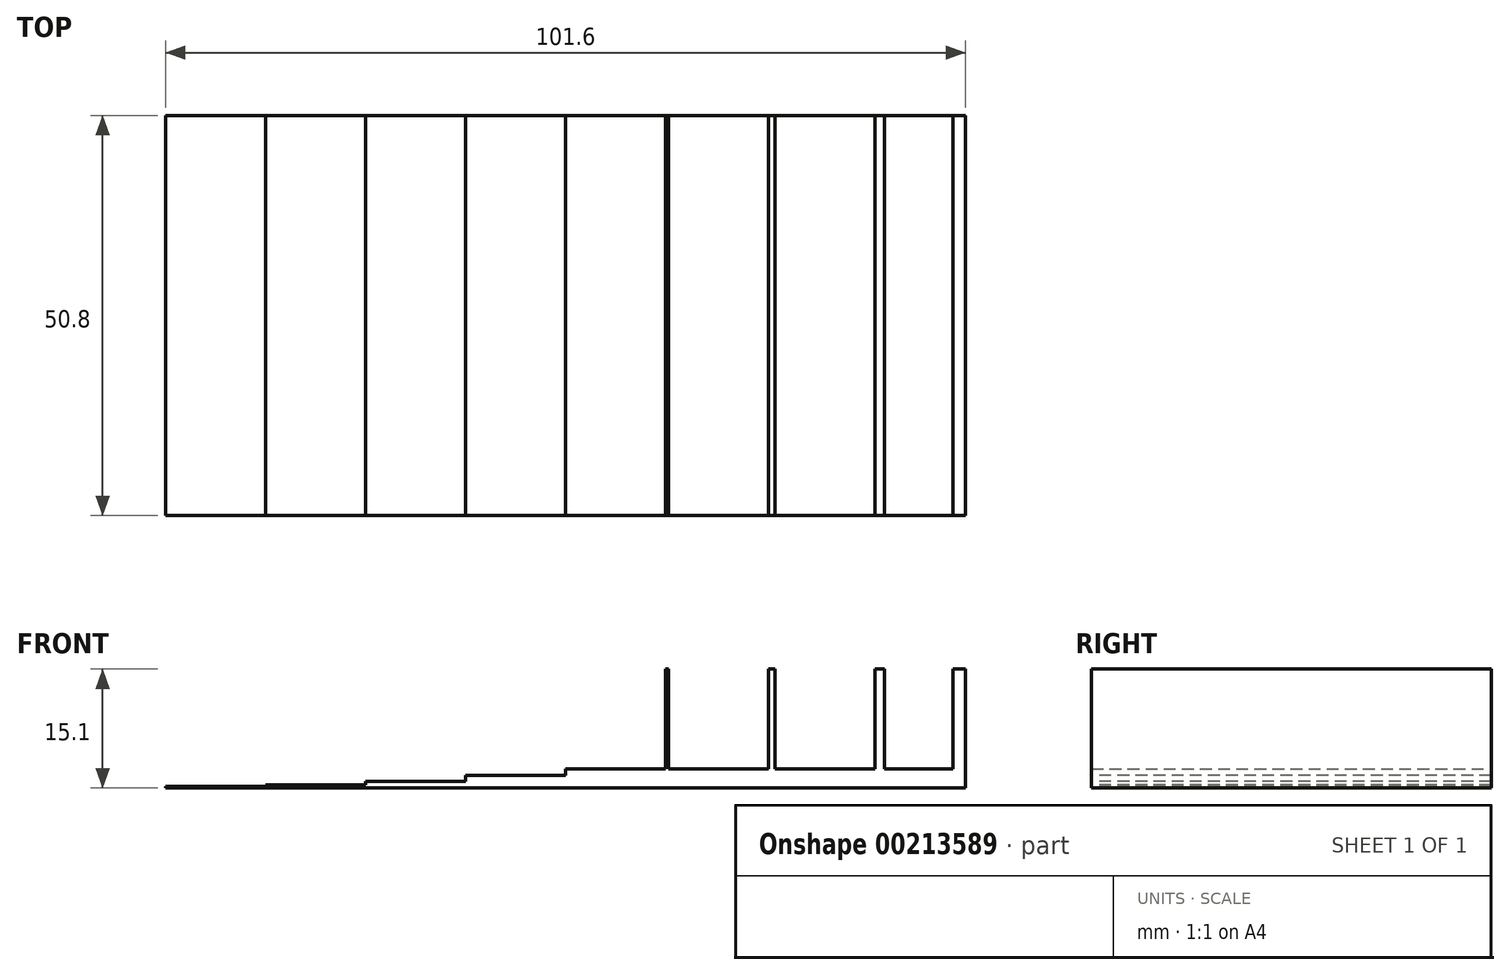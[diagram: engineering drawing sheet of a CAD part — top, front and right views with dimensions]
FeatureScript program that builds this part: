
annotation { "Feature Type Name" : "Feature", "Feature Type Description" : "" }
export const myFeature = defineFeature(function(context is Context, id is Id, definition is map)
    precondition{}
    {
        {
            var Q0;
            Q0=qCreatedBy(makeId("Top.planeOp"),FACE);
            var sketch = newSketch(context, id + "F0", { "sketchPlane" : qUnion([Q0])});
            skLineSegment(sketch, "E0.bottom", {"start": v(-50.8, 25.4) * mm, "end": v(50.8, 25.4) * mm});
            skLineSegment(sketch, "E0.top", {"start": v(-50.8, -25.4) * mm, "end": v(50.8, -25.4) * mm});
            skLineSegment(sketch, "E0.left", {"start": v(-50.8, 25.4) * mm, "end": v(-50.8, -25.4) * mm});
            skLineSegment(sketch, "E0.right", {"start": v(50.8, 25.4) * mm, "end": v(50.8, -25.4) * mm});
            skLineSegment(sketch, "E1", {"start": v(-50.8, 0) * mm, "end": v(50.8, 0) * mm, "construction": true});
            skPoint(sketch, "E2", {"position": v(0, 0) * mm});
            skSolve(sketch);
        }
        {
            var Q0;
            Q0 = qSketchRegion(id + "F0", true);
            extrude(context, id + "F1", {"entities" : qUnion([Q0]), "depth" : .2 * mm});
        }
        {
            var Q0;
            Q0=makeQuery(id+"F1.opExtrude","CAP_FACE",FACE,{"disambiguationData":[OSD([sQuery(id+"F0.wireOp",EDGE,"E0.bottom"),sQuery(id+"F0.wireOp",EDGE,"E0.top"),sQuery(id+"F0.wireOp",EDGE,"E0.left"),sQuery(id+"F0.wireOp",EDGE,"E0.right")])],"isStart":false});
            var sketch = newSketch(context, id + "F2", { "sketchPlane" : qUnion([Q0])});
            skLineSegment(sketch, "E3.bottom", {"start": v(-38.1, 25.4) * mm, "end": v(50.8, 25.4) * mm});
            skLineSegment(sketch, "E3.top", {"start": v(-38.1, -25.4) * mm, "end": v(50.8, -25.4) * mm});
            skLineSegment(sketch, "E3.left", {"start": v(-38.1, 25.4) * mm, "end": v(-38.1, -25.4) * mm});
            skLineSegment(sketch, "E3.right", {"start": v(50.8, 25.4) * mm, "end": v(50.8, -25.4) * mm});
            skSolve(sketch);
        }
        {
            var Q0;
            Q0 = qSketchRegion(id + "F2", true);
            extrude(context, id + "F3", {"entities" : qUnion([Q0]), "operationType" : NewBodyOperationType.ADD, "depth" : .2 * mm});
        }
        {
            var Q0;
            Q0=makeQuery(id+"F3.opExtrude","CAP_FACE",FACE,{"disambiguationData":[OSD([sQuery(id+"F2.wireOp",EDGE,"E3.bottom"),sQuery(id+"F2.wireOp",EDGE,"E3.top"),sQuery(id+"F2.wireOp",EDGE,"E3.left"),sQuery(id+"F2.wireOp",EDGE,"E3.right")])],"isStart":false});
            var sketch = newSketch(context, id + "F4", { "sketchPlane" : qUnion([Q0])});
            skLineSegment(sketch, "E4.bottom", {"start": v(-25.4, 25.4) * mm, "end": v(50.8, 25.4) * mm});
            skLineSegment(sketch, "E4.top", {"start": v(-25.4, -25.4) * mm, "end": v(50.8, -25.4) * mm});
            skLineSegment(sketch, "E4.left", {"start": v(-25.4, 25.4) * mm, "end": v(-25.4, -25.4) * mm});
            skLineSegment(sketch, "E4.right", {"start": v(50.8, 25.4) * mm, "end": v(50.8, -25.4) * mm});
            skSolve(sketch);
        }
        {
            var Q0;
            Q0 = qSketchRegion(id + "F4", true);
            extrude(context, id + "F5", {"entities" : qUnion([Q0]), "operationType" : NewBodyOperationType.ADD, "depth" : .4 * mm});
        }
        {
            var Q0;
            Q0=makeQuery(id+"F5.opExtrude","CAP_FACE",FACE,{"disambiguationData":[OSD([sQuery(id+"F4.wireOp",EDGE,"E4.bottom"),sQuery(id+"F4.wireOp",EDGE,"E4.top"),sQuery(id+"F4.wireOp",EDGE,"E4.left"),sQuery(id+"F4.wireOp",EDGE,"E4.right")])],"isStart":false});
            var sketch = newSketch(context, id + "F6", { "sketchPlane" : qUnion([Q0])});
            skLineSegment(sketch, "E5.bottom", {"start": v(-12.7, 25.4) * mm, "end": v(50.8, 25.4) * mm});
            skLineSegment(sketch, "E5.top", {"start": v(-12.7, -25.4) * mm, "end": v(50.8, -25.4) * mm});
            skLineSegment(sketch, "E5.left", {"start": v(-12.7, 25.4) * mm, "end": v(-12.7, -25.4) * mm});
            skLineSegment(sketch, "E5.right", {"start": v(50.8, 25.4) * mm, "end": v(50.8, -25.4) * mm});
            skSolve(sketch);
        }
        {
            var Q0;
            Q0 = qSketchRegion(id + "F6", true);
            extrude(context, id + "F7", {"entities" : qUnion([Q0]), "operationType" : NewBodyOperationType.ADD, "depth" : .8 * mm});
        }
        {
            var Q0;
            Q0=makeQuery(id+"F7.opExtrude","CAP_FACE",FACE,{"disambiguationData":[OSD([sQuery(id+"F6.wireOp",EDGE,"E5.bottom"),sQuery(id+"F6.wireOp",EDGE,"E5.top"),sQuery(id+"F6.wireOp",EDGE,"E5.left"),sQuery(id+"F6.wireOp",EDGE,"E5.right")])],"isStart":false});
            var sketch = newSketch(context, id + "F8", { "sketchPlane" : qUnion([Q0])});
            skLineSegment(sketch, "E6.bottom", {"start": v(0, 25.4) * mm, "end": v(50.8, 25.4) * mm});
            skLineSegment(sketch, "E6.top", {"start": v(0, -25.4) * mm, "end": v(50.8, -25.4) * mm});
            skLineSegment(sketch, "E6.left", {"start": v(0, 25.4) * mm, "end": v(0, -25.4) * mm});
            skLineSegment(sketch, "E6.right", {"start": v(50.8, 25.4) * mm, "end": v(50.8, -25.4) * mm});
            skSolve(sketch);
        }
        {
            var Q0;
            Q0 = qSketchRegion(id + "F8", true);
            extrude(context, id + "F9", {"entities" : qUnion([Q0]), "operationType" : NewBodyOperationType.ADD, "depth" : .8 * mm});
        }
        {
            var Q0;
            Q0=makeQuery(id+"F9.opExtrude","CAP_FACE",FACE,{"disambiguationData":[OSD([sQuery(id+"F8.wireOp",EDGE,"E6.bottom"),sQuery(id+"F8.wireOp",EDGE,"E6.top"),sQuery(id+"F8.wireOp",EDGE,"E6.left"),sQuery(id+"F8.wireOp",EDGE,"E6.right")])],"isStart":false});
            var sketch = newSketch(context, id + "F10", { "sketchPlane" : qUnion([Q0])});
            skLineSegment(sketch, "E7.bottom", {"start": v(12.7, 25.4) * mm, "end": v(13.1, 25.4) * mm});
            skLineSegment(sketch, "E7.top", {"start": v(12.7, -25.4) * mm, "end": v(13.1, -25.4) * mm});
            skLineSegment(sketch, "E7.left", {"start": v(12.7, 25.4) * mm, "end": v(12.7, -25.4) * mm});
            skLineSegment(sketch, "E7.right", {"start": v(13.1, 25.4) * mm, "end": v(13.1, -25.4) * mm});
            skLineSegment(sketch, "E8.bottom", {"start": v(25.8, 25.4) * mm, "end": v(26.6, 25.4) * mm});
            skLineSegment(sketch, "E8.top", {"start": v(25.8, -25.4) * mm, "end": v(26.6, -25.4) * mm});
            skLineSegment(sketch, "E8.left", {"start": v(25.8, 25.4) * mm, "end": v(25.8, -25.4) * mm});
            skLineSegment(sketch, "E8.right", {"start": v(26.6, 25.4) * mm, "end": v(26.6, -25.4) * mm});
            skLineSegment(sketch, "E9.bottom", {"start": v(39.3, 25.4) * mm, "end": v(40.5, 25.4) * mm});
            skLineSegment(sketch, "E9.top", {"start": v(39.3, -25.4) * mm, "end": v(40.5, -25.4) * mm});
            skLineSegment(sketch, "E9.left", {"start": v(39.3, 25.4) * mm, "end": v(39.3, -25.4) * mm});
            skLineSegment(sketch, "E9.right", {"start": v(40.5, 25.4) * mm, "end": v(40.5, -25.4) * mm});
            skLineSegment(sketch, "E10.bottom", {"start": v(50.8, -25.4) * mm, "end": v(49.2, -25.4) * mm});
            skLineSegment(sketch, "E10.top", {"start": v(50.8, 25.4) * mm, "end": v(49.2, 25.4) * mm});
            skLineSegment(sketch, "E10.left", {"start": v(50.8, -25.4) * mm, "end": v(50.8, 25.4) * mm});
            skLineSegment(sketch, "E10.right", {"start": v(49.2, -25.4) * mm, "end": v(49.2, 25.4) * mm});
            skSolve(sketch);
        }
        {
            var Q0;
            Q0 = qSketchRegion(id + "F10", true);
            extrude(context, id + "F11", {"entities" : qUnion([Q0]), "operationType" : NewBodyOperationType.ADD, "depth" : 12.7 * mm});
        }
    });
